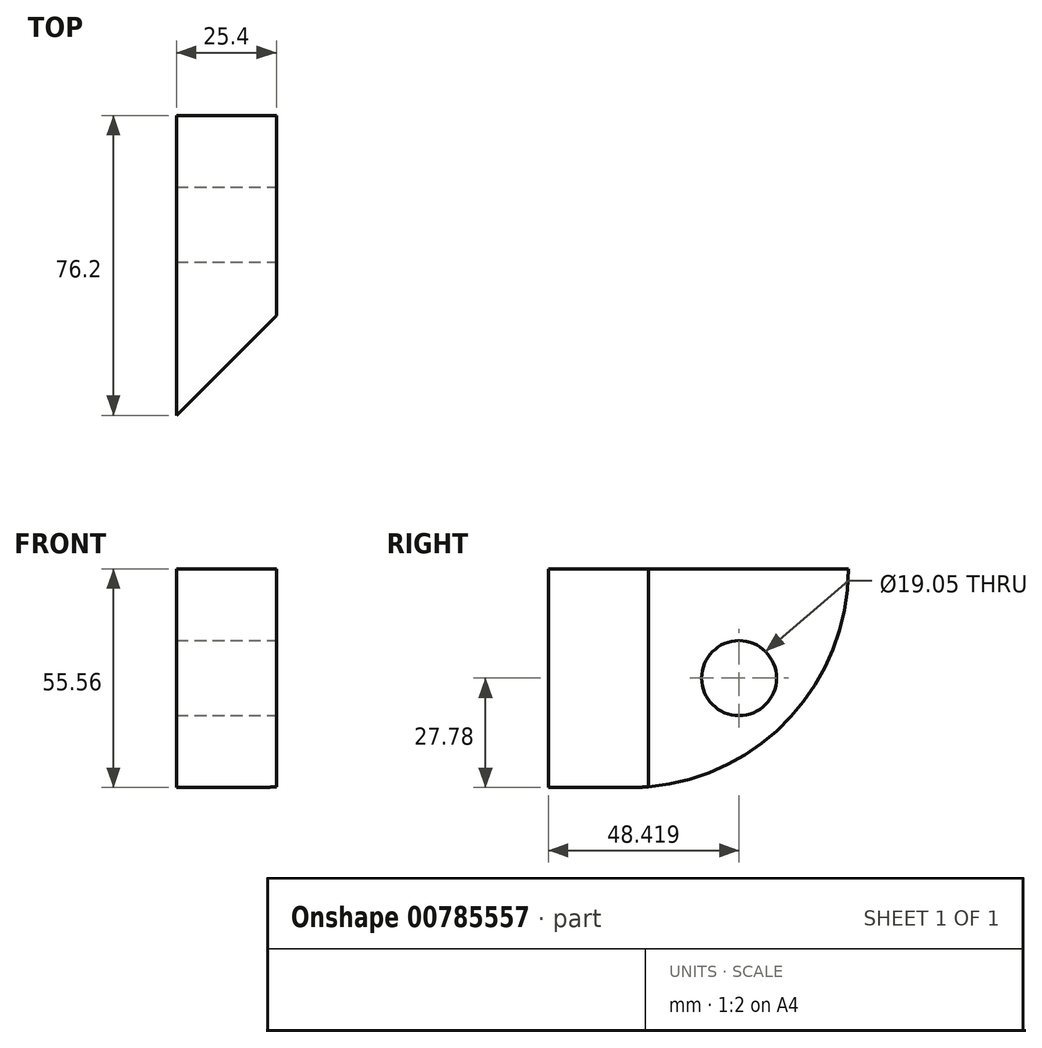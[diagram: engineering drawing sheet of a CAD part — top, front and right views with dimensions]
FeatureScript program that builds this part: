
annotation { "Feature Type Name" : "Feature", "Feature Type Description" : "" }
export const myFeature = defineFeature(function(context is Context, id is Id, definition is map)
    precondition{}
    {
        {
            var Q0;
            Q0=qCreatedBy(makeId("Right.planeOp"),FACE);
            var sketch = newSketch(context, id + "F0", { "sketchPlane" : qUnion([Q0])});
            skLineSegment(sketch, "E0.bottom", {"start": v(38.1, 27.78) * mm, "end": v(-38.1, 27.78) * mm});
            skLineSegment(sketch, "E0.top", {"start": v(38.1, -27.78) * mm, "end": v(-38.1, -27.78) * mm});
            skLineSegment(sketch, "E0.left", {"start": v(38.1, 27.78) * mm, "end": v(38.1, -27.78) * mm});
            skLineSegment(sketch, "E0.right", {"start": v(-38.1, 27.78) * mm, "end": v(-38.1, -27.78) * mm});
            skPoint(sketch, "E0.middle", {"position": v(0, 0) * mm});
            skSolve(sketch);
        }
        {
            var Q0;
            Q0 = qSketchRegion(id + "F0", true);
            extrude(context, id + "F1", {"entities" : qUnion([Q0]), "depth" : 25.4 * mm, "offsetDistance" : 25.4 * mm});
        }
        {
            var Q0;
            Q0=makeQuery(id+"F1.opExtrude","SWEPT_EDGE",EDGE,{"disambiguationData":[OSD([sQuery(id+"F0.wireOp",EDGE,"E0.top"),sQuery(id+"F0.wireOp",EDGE,"E0.left")])]});
            fillet(context, id + "F2", {"entities" : qUnion([Q0]), "radius" : 55.56 * mm, "tangentPropagation" : true, "allowEdgeOverflow" : false});
        }
        {
            var Q0;
            Q0=makeQuery(id+"F1.opExtrude","CAP_FACE",FACE,{"disambiguationData":[OSD([sQuery(id+"F0.wireOp",EDGE,"E0.bottom"),sQuery(id+"F0.wireOp",EDGE,"E0.top"),sQuery(id+"F0.wireOp",EDGE,"E0.left"),sQuery(id+"F0.wireOp",EDGE,"E0.right")])],"isStart":false});
            var sketch = newSketch(context, id + "F3", { "sketchPlane" : qUnion([Q0])});
            skLineSegment(sketch, "E1", {"start": v(-17.46, -27.78) * mm, "end": v(38.1, 27.78) * mm});
            skCircle(sketch, "E2", {"center": v(10.32, 0) * mm, "radius": 9.53 * mm});
            skSolve(sketch);
        }
        {
            var Q0;
            Q0 = qSketchRegion(id + "F3", true);
            extrude(context, id + "F4", {"entities" : qUnion([Q0]), "operationType" : NewBodyOperationType.REMOVE, "oppositeDirection" : true, "depth" : 25.4 * mm, "offsetDistance" : 25.4 * mm});
        }
        {
            var Q0;
            Q0=makeQuery(id+"F1.opExtrude","SWEPT_FACE",FACE,{"disambiguationData":[OSD([sQuery(id+"F0.wireOp",EDGE,"E0.bottom")])]});
            var sketch = newSketch(context, id + "F5", { "sketchPlane" : qUnion([Q0])});
            skLineSegment(sketch, "E3", {"start": v(0, -38.1) * mm, "end": v(25.4, -12.7) * mm});
            skSolve(sketch);
        }
        {
            var Q0;
            Q0 = qSketchRegion(id + "F5", true);
            var Q1;
            {var subQ0=sQuery(id+"F5.wireOp",EDGE,"E3");Q1=makeQuery(id+"F5.imprint","IMPRINT",FACE,{"disambiguationData":[TD([[makeQuery(id+"F5.imprint","IMPRINT",EDGE,{"derivedFrom":subQ0}),-1.0]])]});}
            extrude(context, id + "F6", {"entities" : qUnion([Q0, Q1]), "operationType" : NewBodyOperationType.REMOVE, "endBound" : BoundingType.THROUGH_ALL, "oppositeDirection" : true, "depth" : 25.4 * mm, "offsetDistance" : 25.4 * mm});
        }
    });
